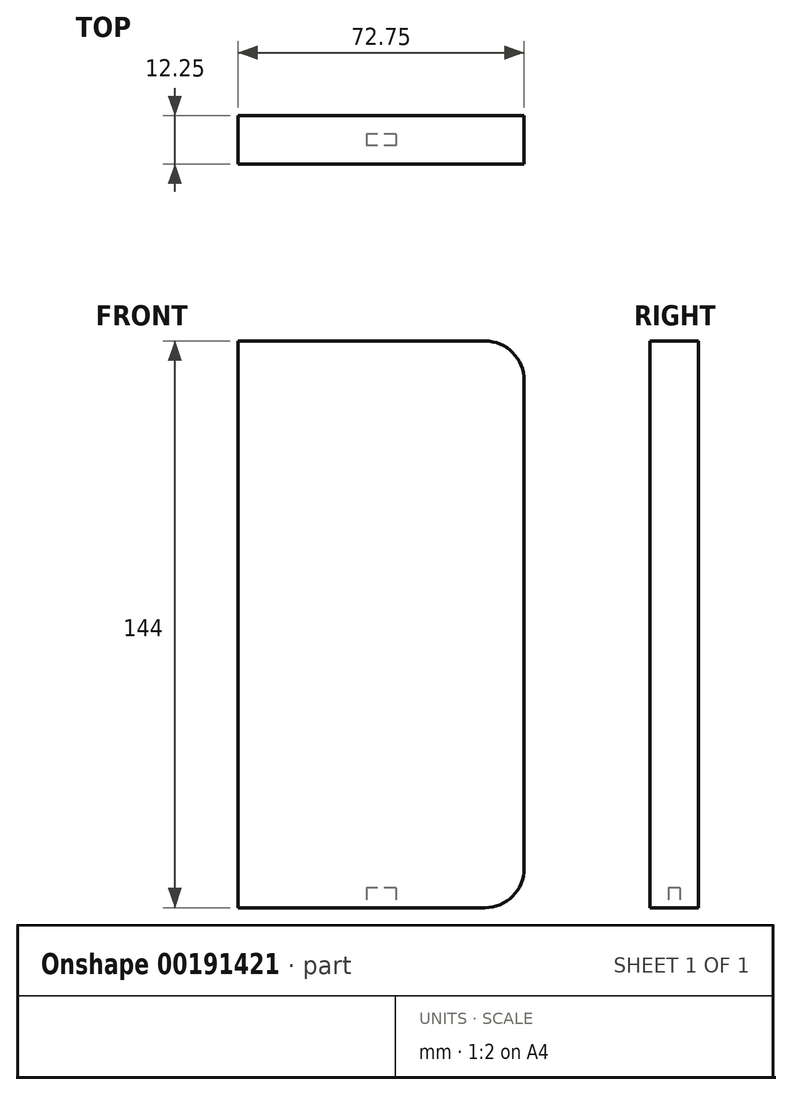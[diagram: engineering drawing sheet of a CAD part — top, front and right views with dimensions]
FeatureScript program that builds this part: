
annotation { "Feature Type Name" : "Feature", "Feature Type Description" : "" }
export const myFeature = defineFeature(function(context is Context, id is Id, definition is map)
    precondition{}
    {
        {
            var Q0;
            Q0=qCreatedBy(makeId("Front.planeOp"),FACE);
            var sketch = newSketch(context, id + "F0", { "sketchPlane" : qUnion([Q0])});
            skLineSegment(sketch, "E0.bottom", {"start": v(62.75, 144) * mm, "end": v(0, 144) * mm});
            skLineSegment(sketch, "E0.top", {"start": v(62.75, 0) * mm, "end": v(0, 0) * mm});
            skLineSegment(sketch, "E0.left", {"start": v(72.75, 134) * mm, "end": v(72.75, 10) * mm});
            skLineSegment(sketch, "E0.right", {"start": v(0, 144) * mm, "end": v(0, 0) * mm});
            skPoint(sketch, "E1.visualSharp", {"position": v(72.75, 144) * mm});
            skArc(sketch, "E1.filletArc", {"start": v(72.75, 134) * mm, "mid": v(69.82, 141.07) * mm, "end": v(62.75, 144) * mm});
            skPoint(sketch, "E2.visualSharp", {"position": v(72.75, 0) * mm});
            skArc(sketch, "E2.filletArc", {"start": v(62.75, 0) * mm, "mid": v(69.82, 2.93) * mm, "end": v(72.75, 10) * mm});
            skSolve(sketch);
        }
        {
            var Q0;
            Q0=makeQuery(id+"F0.imprint","IMPRINT",FACE,{"disambiguationData":[TD([[makeQuery(id+"F0.imprint","IMPRINT",EDGE,{"derivedFrom":sQuery(id+"F0.wireOp",EDGE,"E0.bottom")}),1.0]])]});
            extrude(context, id + "F1", {"entities" : qUnion([Q0]), "depth" : 12.25 * mm});
        }
        {
            var Q0;
            Q0=makeQuery(id+"F1.opExtrude","SWEPT_FACE",FACE,{"disambiguationData":[OSD([sQuery(id+"F0.wireOp",EDGE,"E0.top")])]});
            var sketch = newSketch(context, id + "F2", { "sketchPlane" : qUnion([Q0])});
            skLineSegment(sketch, "E3", {"start": v(0, 6.12) * mm, "end": v(72.75, 6.12) * mm, "construction": true});
            skLineSegment(sketch, "E4.bottom", {"start": v(40.13, 4.62) * mm, "end": v(32.63, 4.62) * mm});
            skLineSegment(sketch, "E4.top", {"start": v(40.13, 7.62) * mm, "end": v(32.63, 7.62) * mm});
            skLineSegment(sketch, "E4.left", {"start": v(40.13, 4.62) * mm, "end": v(40.13, 7.62) * mm});
            skLineSegment(sketch, "E4.right", {"start": v(32.63, 4.62) * mm, "end": v(32.63, 7.62) * mm});
            skPoint(sketch, "E4.middle", {"position": v(36.38, 6.12) * mm});
            skSolve(sketch);
        }
        {
            var Q0;
            Q0 = qSketchRegion(id + "F2", true);
            extrude(context, id + "F3", {"entities" : qUnion([Q0]), "operationType" : NewBodyOperationType.REMOVE, "oppositeDirection" : true, "depth" : 5 * mm});
        }
    });
